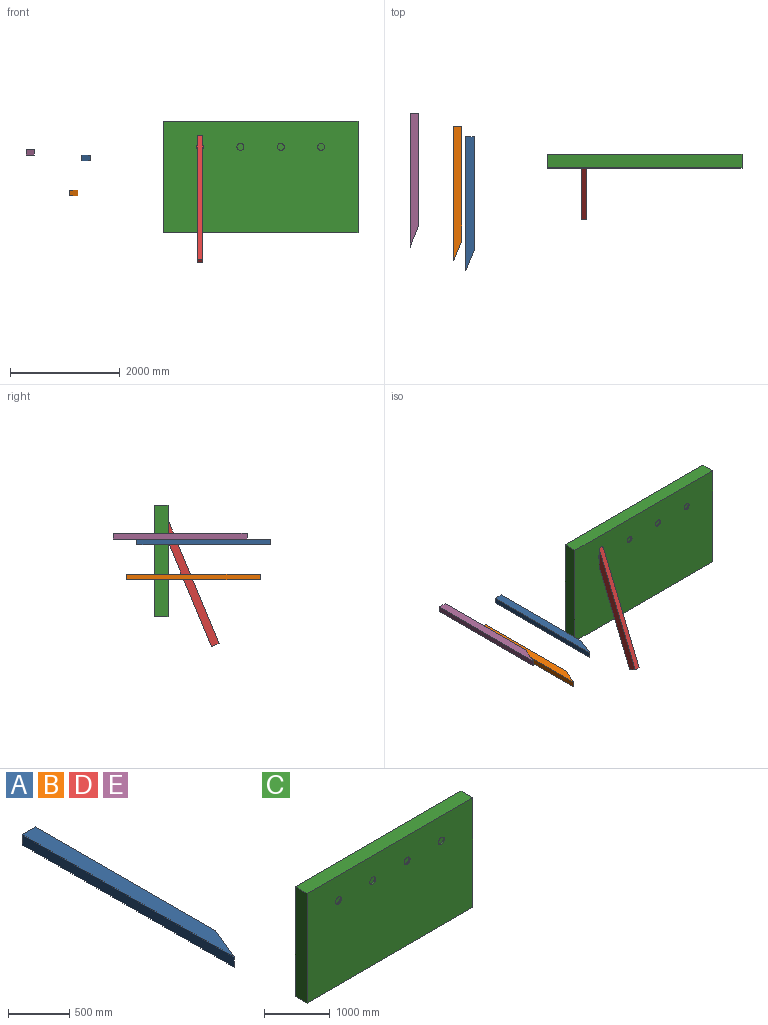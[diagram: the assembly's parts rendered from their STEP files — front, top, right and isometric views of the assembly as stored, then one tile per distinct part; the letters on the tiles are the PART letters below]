
ASSEMBLY  parts=5 mates=1
PART A: 6 faces, bbox 152.4x2438.4x101.6 mm
  f0: plane 2438.4x152.4mm, normal (0,0,-1), area 343576.2mm2, adj f1,f3,f4,f5
  f1: plane 2070.47x101.6mm, normal (1,0,0), area 210360.1mm2, adj f0,f2,f4,f5
  f2: plane 2438.4x152.4mm, normal (0,0,1), area 343576.2mm2, adj f1,f3,f4,f5
  f3: plane 2438.4x101.6mm, normal (-1,0,0), area 247741.4mm2, adj f0,f2,f4,f5
  f4: plane 152.4x101.6mm, normal (0,1,0), area 15483.8mm2, adj f0,f1,f2,f3
  f5: plane 367.93x152.4mm, normal (0.92,-0.38,0), area 40461.2mm2, adj f0,f1,f2,f3
PART B: same geometry as A
PART C: 14 faces, bbox 3556x254x2032 mm
  f0: plane 3556x254mm, normal (0,0,1), area 903224mm2, adj f1,f3,f4,f5
  f1: plane 2032x254mm, normal (-1,0,0), area 516128mm2, adj f0,f2,f4,f5
  f2: plane 3556x254mm, normal (0,0,-1), area 903224mm2, adj f1,f3,f4,f5
  f3: plane 2032x254mm, normal (1,0,0), area 516128mm2, adj f0,f2,f4,f5
  f4: plane 3556x2032mm, normal (0,-1,0), area 7175121.3mm2, adj f0,f1,f2,f3,f6,f8,f10,f12
  f5: plane 3556x2032mm, normal (0,1,0), area 7225792mm2, adj f0,f1,f2,f3
  f6: cylinder r=63.5mm len=127mm, axis (0,-1,0), area 10134.1mm2, adj f4,f7
  f7: plane 127x127mm, normal (0,-1,0), area 12667.7mm2, adj f6
  f8: cylinder r=63.5mm len=127mm, axis (0,-1,0), area 10134.1mm2, adj f4,f9
  f9: plane 127x127mm, normal (0,-1,0), area 12667.7mm2, adj f8
  f10: cylinder r=63.5mm len=127mm, axis (0,-1,0), area 10134.1mm2, adj f4,f11
  f11: plane 127x127mm, normal (0,-1,0), area 12667.7mm2, adj f10
  f12: cylinder r=63.5mm len=127mm, axis (0,-1,0), area 10134.1mm2, adj f4,f13
  f13: plane 127x127mm, normal (0,-1,0), area 12667.7mm2, adj f12
PART D: same geometry as A
PART E: same geometry as A
PLACE A t=(-2987.78,567.34,342.42)mm
PLACE B t=(-3209.37,757.2,-301.02)mm
PLACE C t=(-26.13,254,555.51)mm
PLACE D rot(axis=(-0.64,-0.43,0.64),133.7deg) t=(-1091.31,-676.86,-1604.31)mm
PLACE E t=(-4005.52,996.72,444.28)mm
MATE fastened D.f5 <-> C.f12  axis (0,1,0) through (-1104.9,0,555.51)mm
